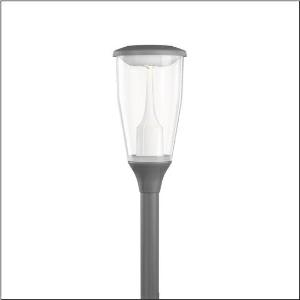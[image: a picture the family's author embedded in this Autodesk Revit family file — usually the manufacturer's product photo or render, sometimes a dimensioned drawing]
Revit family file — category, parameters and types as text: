
# Revit family: dl_11_iq___st1_2a_5xa5575ef14h000022_0b87
name_source: partatom
category: Lighting Fixtures
units: mm (PartAtom-declared; Revit-internal decimal feet)

## family parameters
Cut with Voids When Loaded = No
Host = Face
Light Source = No
Part Type = Normal
Room Calculation Point = No
Round Connector Dimension = Use Diameter
Shared = No

## types (1)
- --- (1 x LED, 1560 lm, 10.5 W, 3000K)
    Apparent Load = 11 VA
    CIE Flux Codes = 24 63 94 96 100
    Color Rendering = 70
    Color Temperature = 3000K
    Default Elevation = 1800 mm
    Description = DL 11 iQ, mast luminaire, Module 540 iQ-SR, primary light control with 3 zone facetted reflector, of plastic, silver coated, highly specular, structured, primary optical cover: cover, of PMMA, transparent, light distribution: ST1.2a, light emission: direct distribution, primary light characteristic: asymmetric, installation type: post-top, LED, High Power LED, rated luminous flux: 1.560lm, luminous efficacy: 149lm/W, light colour: 730, colour temperature: 3000K, control: Street-Remote, Auto-Match, Temp-Guard, Lumen-Switch, Night-Set, Smart-Wire, Light-Fading, Desk-Remote (wireless, voltage-free reading and setting of iQ features in the workshop via application-optimized NFC function/RFID function), optimised constant luminous flux control (CLO 2.0), mains connection: 220..240V, AC, 50/60Hz, connection cable pre-assembled, cable length: 5,5m, start of lifetime: 11W, end of service life: 11W, reduction: 5W, luminaire housing, upper part, of diecast aluminium, coated, Siteco® metallic grey (DB 702S), spigot size: 76mm (post-top), post-top mast mounting element, of diecast aluminium, coated, Siteco® metallic grey (DB 702S), Module 540 iQ-SR, traffic white (RAL 9016), equipment: standard, protection rating (complete): IP66, insulation class (complete): insulation class II (safety insulation), certification: CE, ENEC, ENEC+, VDE, packaging unit: 1 piece

Light Distribution: ST1.2a
    Height = 665 mm
    Lamp = 1 x LED
    Lamp Light Flux = 1560 lm
    Lamp Power = 10.5 W
    Lamp count = 1
    Length = 334 mm
    Luminous efficacy = 149 lm/W
    Manufacturer = Siteco
    ModVariant = No
    Model = 5XA5575EF14H000022
    Number of Poles = 1
    OnlyDefault = Yes
    Power Factor = 1
    Product Name = DL 11 iQ | ST1.2a
    Product group = mast luminaire | pylon top
    ProductGroupID = 6100
    Protection Class = Protection class II
    Protection Degree = IP 66
    RLX_Detail_Level = 1
    RLX_Emergency_Light_Flux = 0 lm
    RLX_Emergency_Type = 0
    RLX_Emergency_Type_DB = No
    RlxData = <blob elided: 152673 chars, md5=fd3de69f>
    Socket = socket
    Standby Power = 0 W
    System Light Flux = 1560 lm
    System Power = 11 W
    Type Comments = factory setting: luminous flux: 100 % | dim-lin: 254 | 419 mA
    Type Image = l_1258354.jpg
    URL = http://relux.com
    VarID = @adj_043931
    Voltage = 0 V
    Weight = 0.00 kg
    Width = 0 mm  [stored 0 ft]

note: [stored X ft] marks values corroborated as IEEE doubles in the binary element streams (Revit-internal decimal feet)

## geometry (parser evidence)
native form markers: Blend x4, Sweep x8
no freeform markers — native parametric forms only
